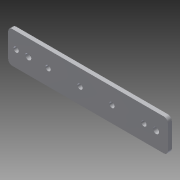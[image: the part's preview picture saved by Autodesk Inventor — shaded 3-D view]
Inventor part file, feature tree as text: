
AUTODESK INVENTOR PART (.ipt)
format: ipt  version: 2014 (Build 180170000, 170)  size: 98,816 bytes
history: native  units: in
note: dims shown in document units (in); Inventor stores cm internally (conversion verified against a paired STEP export)
features: extrude x1, fillet x1, sketch x1
ambient origin geometry x8: Origin, YZ Plane, XZ Plane, XY Plane, X Axis, Y Axis, Z Axis, Center Point
bodies: Solid1 (feature_tree)
feature tree (3):
  extrude  "Extrusion1"  Depth=1.0in
  fillet  "Fillet1"  Radius=0.163in
  sketch  "Sketch1"  dims[d0=5.0in d1=1.0in d2=0.163in d3=0.5in d4=0.25in d5=1.9685in d7=1.0in d8=0.3937in d10=1.0in d12=0.19in d13=0.7874in d15=4.0in d16=0.3937in d18=1.0in d21=0.38in d22=0.5in d23=0.125in d24=0.0in d25=0.125in]
